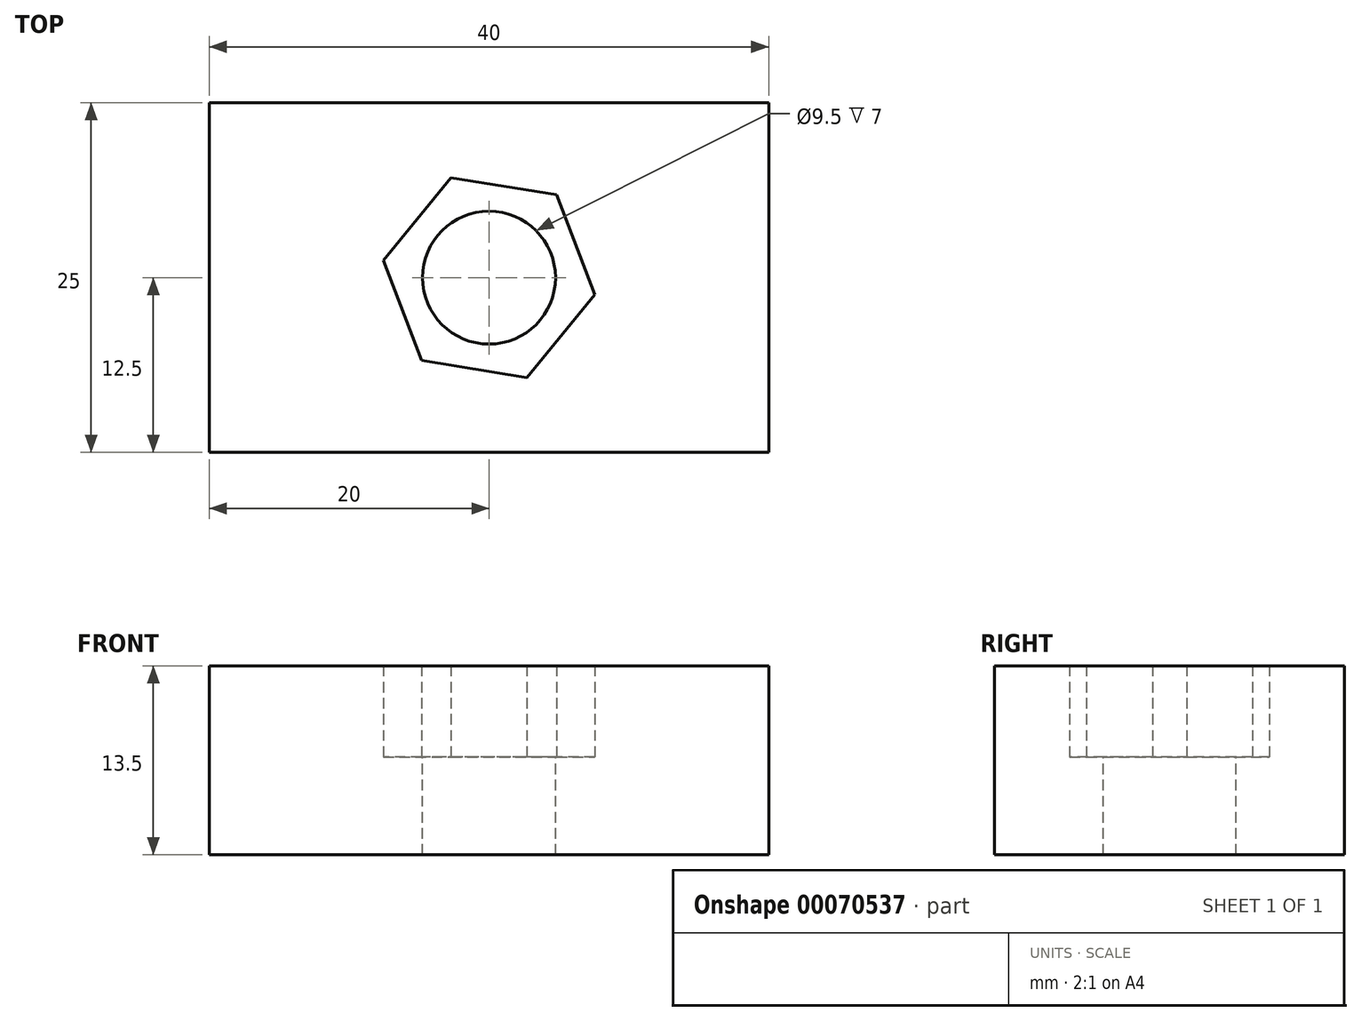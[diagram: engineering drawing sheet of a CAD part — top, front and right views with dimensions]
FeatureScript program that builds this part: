
annotation { "Feature Type Name" : "Feature", "Feature Type Description" : "" }
export const myFeature = defineFeature(function(context is Context, id is Id, definition is map)
    precondition{}
    {
        {
            var Q0;
            Q0=qCreatedBy(makeId("Top.planeOp"),FACE);
            var sketch = newSketch(context, id + "F0", { "sketchPlane" : qUnion([Q0])});
            skPoint(sketch, "E0.rect.middle", {"position": v(0, 0) * mm});
            skCircle(sketch, "E1.cCircle", {"center": v(0, 0) * mm, "radius": 6.62 * mm, "construction": true});
            skLineSegment(sketch, "E1.0", {"start": v(4.84, 5.93) * mm, "end": v(7.55, -1.22) * mm});
            skLineSegment(sketch, "E1.1", {"start": v(7.55, -1.22) * mm, "end": v(2.72, -7.15) * mm});
            skLineSegment(sketch, "E1.2", {"start": v(2.72, -7.15) * mm, "end": v(-4.84, -5.93) * mm});
            skLineSegment(sketch, "E1.3", {"start": v(-4.84, -5.93) * mm, "end": v(-7.55, 1.22) * mm});
            skLineSegment(sketch, "E1.4", {"start": v(-7.55, 1.22) * mm, "end": v(-2.72, 7.15) * mm});
            skLineSegment(sketch, "E1.5", {"start": v(-2.72, 7.15) * mm, "end": v(4.84, 5.93) * mm});
            skPoint(sketch, "E1.0.midPoint", {"position": v(6.2, 2.35) * mm});
            skLineSegment(sketch, "E2.rect.bottom", {"start": v(20, -12.5) * mm, "end": v(-20, -12.5) * mm});
            skLineSegment(sketch, "E2.rect.top", {"start": v(20, 12.5) * mm, "end": v(-20, 12.5) * mm});
            skLineSegment(sketch, "E2.rect.left", {"start": v(20, -12.5) * mm, "end": v(20, 12.5) * mm});
            skLineSegment(sketch, "E2.rect.right", {"start": v(-20, -12.5) * mm, "end": v(-20, 12.5) * mm});
            skSolve(sketch);
        }
        {
            var Q0;
            Q0=makeQuery(id+"F0.imprint","IMPRINT",FACE,{"disambiguationData":[TD([[makeQuery(id+"F0.imprint","IMPRINT",EDGE,{"derivedFrom":sQuery(id+"F0.wireOp",EDGE,"E1.0")}),1.0]])]});
            var Q1;
            Q1=makeQuery(id+"F0.imprint","IMPRINT",FACE,{"disambiguationData":[TD([[makeQuery(id+"F0.imprint","IMPRINT",EDGE,{"derivedFrom":sQuery(id+"F0.wireOp",EDGE,"E1.0")}),-1.0]])]});
            extrude(context, id + "F1", {"entities" : qUnion([Q0, Q1]), "oppositeDirection" : true, "depth" : 7 * mm});
        }
        {
            var sketch = newSketch(context, id + "F2", { "sketchPlane" : qUnion([])});
            skPoint(sketch, "E3.rect.middle", {"position": v(-0.44, -0.17) * mm});
            skCircle(sketch, "E4.cCircle", {"center": v(-0.44, -0.17) * mm, "radius": 6.62 * mm, "construction": true});
            skLineSegment(sketch, "E4.0", {"start": v(4.4, 5.76) * mm, "end": v(7.1, -1.4) * mm});
            skLineSegment(sketch, "E4.1", {"start": v(7.1, -1.4) * mm, "end": v(2.27, -7.32) * mm});
            skLineSegment(sketch, "E4.2", {"start": v(2.27, -7.32) * mm, "end": v(-5.28, -6.1) * mm});
            skLineSegment(sketch, "E4.3", {"start": v(-5.28, -6.1) * mm, "end": v(-8, 1.06) * mm});
            skLineSegment(sketch, "E4.4", {"start": v(-8, 1.06) * mm, "end": v(-3.16, 6.98) * mm});
            skLineSegment(sketch, "E4.5", {"start": v(-3.16, 6.98) * mm, "end": v(4.4, 5.76) * mm});
            skPoint(sketch, "E4.0.midPoint", {"position": v(5.75, 2.18) * mm});
            skLineSegment(sketch, "E5.rect.bottom", {"start": v(19.56, -12.67) * mm, "end": v(-20.44, -12.67) * mm});
            skLineSegment(sketch, "E5.rect.top", {"start": v(19.56, 12.33) * mm, "end": v(-20.44, 12.33) * mm});
            skLineSegment(sketch, "E5.rect.left", {"start": v(19.56, -12.67) * mm, "end": v(19.56, 12.33) * mm});
            skLineSegment(sketch, "E5.rect.right", {"start": v(-20.44, -12.67) * mm, "end": v(-20.44, 12.33) * mm});
            skSolve(sketch);
        }
        {
            var Q0;
            Q0 = qSketchRegion(id + "F2", true);
            var Q1;
            Q1=makeQuery(id+"F0.imprint","IMPRINT",FACE,{"disambiguationData":[TD([[makeQuery(id+"F0.imprint","IMPRINT",EDGE,{"derivedFrom":sQuery(id+"F0.wireOp",EDGE,"E1.0")}),1.0]])]});
            extrude(context, id + "F3", {"entities" : qUnion([Q0, Q1]), "operationType" : NewBodyOperationType.ADD, "depth" : 6.5 * mm});
        }
        {
            var Q0;
            Q0=qCreatedBy(makeId("Top.planeOp"),FACE);
            var sketch = newSketch(context, id + "F4", { "sketchPlane" : qUnion([Q0])});
            skCircle(sketch, "E6", {"center": v(0, 0) * mm, "radius": 4.75 * mm});
            skSolve(sketch);
        }
        {
            var Q0;
            Q0 = qSketchRegion(id + "F4", true);
            extrude(context, id + "F5", {"entities" : qUnion([Q0]), "operationType" : NewBodyOperationType.REMOVE, "oppositeDirection" : true, "depth" : 10 * mm});
        }
    });
